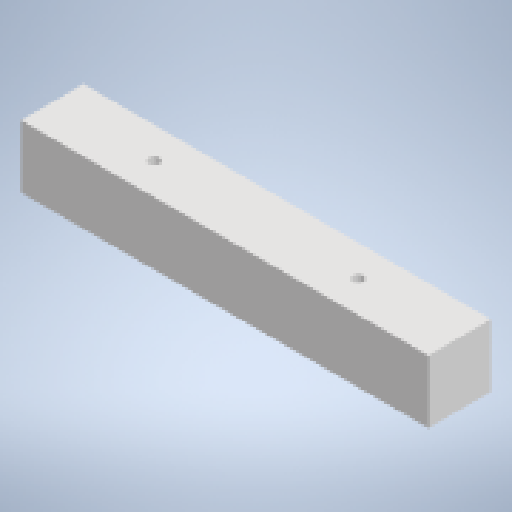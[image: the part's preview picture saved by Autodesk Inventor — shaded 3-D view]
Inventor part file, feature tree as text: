
AUTODESK INVENTOR PART (.ipt)
format: ipt  version: 2024 (Build 280153000, 153)  size: 222,720 bytes
history: native  units: mm
features: sketch x2, extrude x1, hole x1
ambient origin geometry x8: Origin, YZ Plane, XZ Plane, XY Plane, X Axis, Y Axis, Z Axis, Center Point
bodies: Body1 (feature_tree)
feature tree (4):
  extrude  "돌출2"  Depth=130.0mm
  hole  "구멍1"  [1 undecoded]
  sketch  "스케치2"
  sketch  "스케치3"
note: 1 required parameter value undecoded (feature->parameter linkage not recoverable at this tier; creation-order binding heuristic only, values carry confidence <= 0.55)
